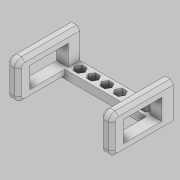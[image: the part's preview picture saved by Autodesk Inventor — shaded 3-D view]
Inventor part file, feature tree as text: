
AUTODESK INVENTOR PART (.ipt)
format: ipt  version: 2022.2 (Build 262287010, 287A)  size: 221,184 bytes
history: native  units: mm
features: extrude x4, sketch x4, other x1, fillet x1, chamfer x1
ambient origin geometry x8: Origin, YZ Plane, XZ Plane, XY Plane, X Axis, Y Axis, Z Axis, Center Point
bodies: Body1 (feature_tree)
feature tree (11):
  other  "Sólido1"
  extrude  "Extrusión1"  Depth=7.0mm
  extrude  "Extrusión7"  Depth=17.5mm TaperAngle=0.0deg
  extrude  "Extrusión8"  Depth=23.0mm
  fillet  "Empalme5"  [1 undecoded]
  chamfer  "Chaflán3"  Distance=2.0mm Angle=45.0deg
  extrude  "Extrusión9"  Depth=10.0mm
  sketch  "Boceto1"  dims[d14=5.0mm d15=0.0mm d70=7.0mm]
  sketch  "Boceto11"  dims[d71=37.0mm d72=17.5mm d73=0.0mm]
  sketch  "Boceto12"  dims[d74=12.5mm d75=23.0mm d76=0.0mm d77=0.0mm]
  sketch  "Boceto13"  dims[d79=4.0mm d80=2.0mm d81=2.0mm d82=45.0deg d86=31.5mm d87=5.5mm d88=9.0mm d89=4.5mm d90=4.0mm d91=30.0mm d93=8.0mm d94=10.0mm d96=10.0mm d98=10.0mm d99=0.0mm]
note: 1 required parameter value undecoded (feature->parameter linkage not recoverable at this tier; creation-order binding heuristic only, values carry confidence <= 0.55)
